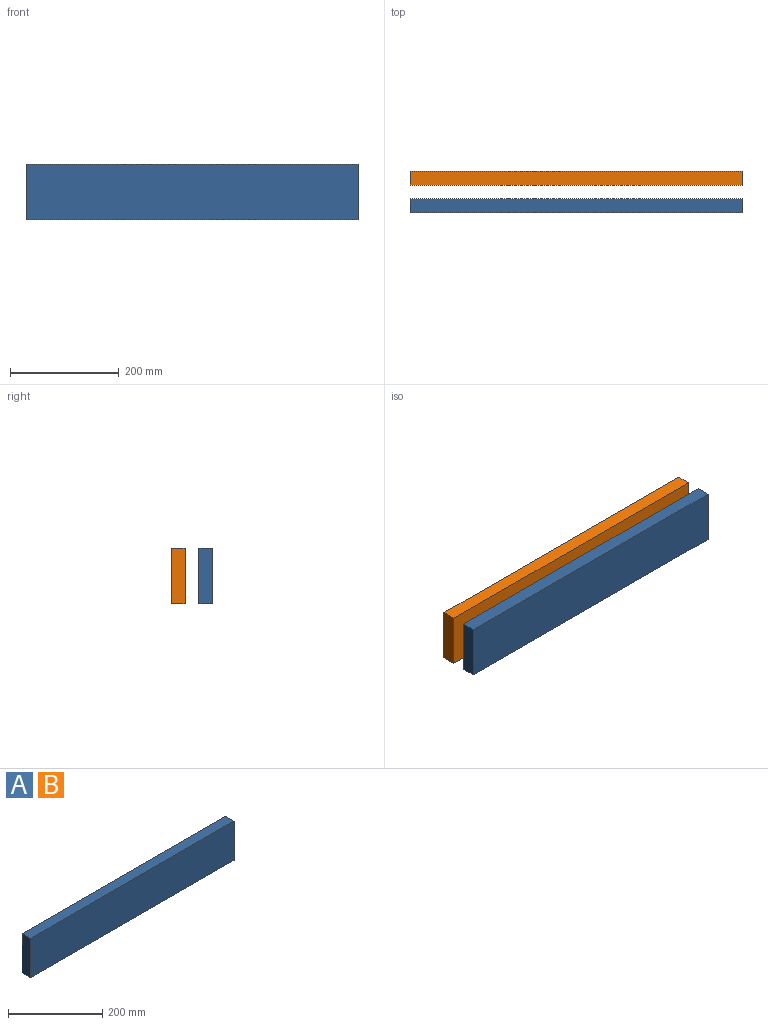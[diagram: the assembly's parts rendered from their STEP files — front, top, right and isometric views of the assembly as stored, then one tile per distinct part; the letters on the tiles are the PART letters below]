
ASSEMBLY  parts=2 mates=1
PART A: 6 faces, bbox 609.6x25.4x101.6 mm
  f0: plane 609.6x25.4mm, normal (0,0,1), area 15483.8mm2, adj f1,f2,f3,f5
  f1: plane 609.6x101.6mm, normal (0,-1,0), area 61935.4mm2, adj f0,f2,f3,f4
  f2: plane 101.6x25.4mm, normal (1,0,0), area 2580.6mm2, adj f0,f1,f4,f5
  f3: plane 101.6x25.4mm, normal (-1,0,0), area 2580.6mm2, adj f0,f1,f4,f5
  f4: plane 609.6x25.4mm, normal (0,0,-1), area 15483.8mm2, adj f1,f2,f3,f5
  f5: plane 609.6x101.6mm, normal (0,1,0), area 61935.4mm2, adj f0,f2,f3,f4
PART B: same geometry as A
PLACE A t=(-26.81,42.51,-47.1)mm
PLACE B t=(-26.81,93.31,-47.1)mm
MATE parallel B.f3 <-> A.f3  axis (1,0,0) through (-331.61,67.91,3.7)mm
